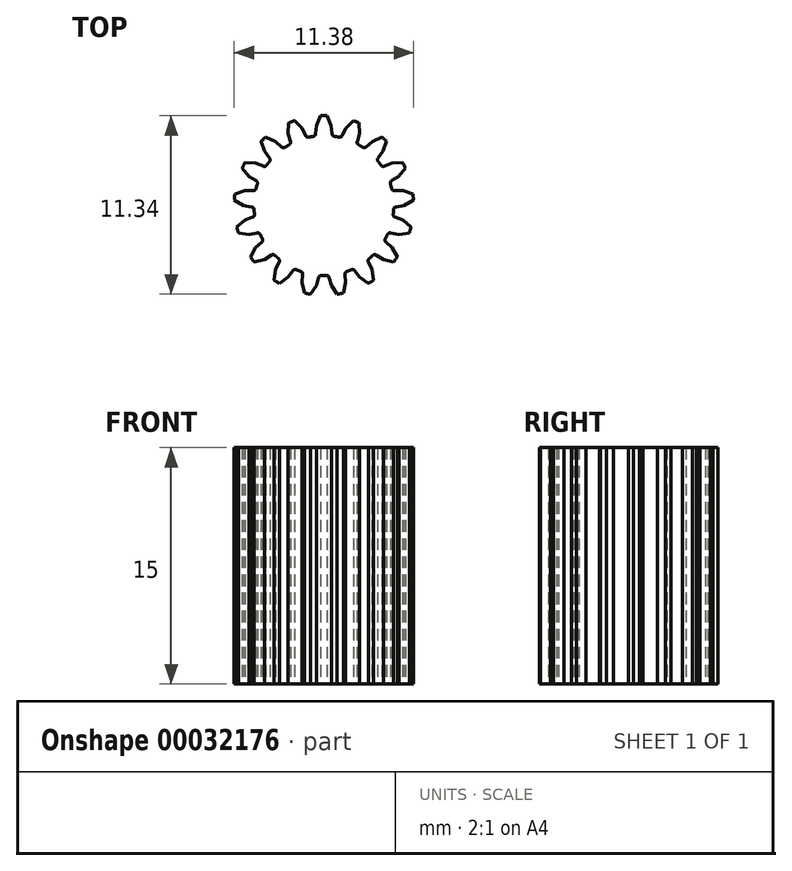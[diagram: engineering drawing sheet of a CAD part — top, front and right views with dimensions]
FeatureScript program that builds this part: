
annotation { "Feature Type Name" : "Feature", "Feature Type Description" : "" }
export const myFeature = defineFeature(function(context is Context, id is Id, definition is map)
    precondition{}
    {
        {
            var Q0;
            Q0=qCreatedBy(makeId("Top.planeOp"),FACE);
            var sketch = newSketch(context, id + "F0", { "sketchPlane" : qUnion([Q0])});
            skLineSegment(sketch, "E0", {"start": v(7.63, -0.2) * mm, "end": v(8.5, -0.04) * mm});
            skLineSegment(sketch, "E1", {"start": v(8.5, -0.04) * mm, "end": v(9.48, 0.5) * mm});
            skArc(sketch, "E2", {"start": v(9.48, 0.5) * mm, "mid": v(9.46, 0.82) * mm, "end": v(9.42, 1.15) * mm});
            skLineSegment(sketch, "E3", {"start": v(9.42, 1.15) * mm, "end": v(8.36, 1.5) * mm});
            skLineSegment(sketch, "E4", {"start": v(8.36, 1.5) * mm, "end": v(7.47, 1.5) * mm});
            skArc(sketch, "E5", {"start": v(7.18, 1.73) * mm, "mid": v(7.29, 1.56) * mm, "end": v(7.47, 1.5) * mm});
            skArc(sketch, "E6", {"start": v(7.18, 1.73) * mm, "mid": v(7.12, 1.97) * mm, "end": v(7.04, 2.21) * mm});
            skArc(sketch, "E7", {"start": v(7.17, 2.56) * mm, "mid": v(7.05, 2.4) * mm, "end": v(7.04, 2.21) * mm});
            skLineSegment(sketch, "E8", {"start": v(7.17, 2.56) * mm, "end": v(7.92, 3.03) * mm});
            skLineSegment(sketch, "E9", {"start": v(7.92, 3.03) * mm, "end": v(8.65, 3.88) * mm});
            skArc(sketch, "E10", {"start": v(8.65, 3.88) * mm, "mid": v(8.5, 4.18) * mm, "end": v(8.35, 4.48) * mm});
            skLineSegment(sketch, "E11", {"start": v(8.35, 4.48) * mm, "end": v(7.23, 4.41) * mm});
            skLineSegment(sketch, "E12", {"start": v(7.23, 4.41) * mm, "end": v(6.4, 4.1) * mm});
            skArc(sketch, "E13", {"start": v(6.05, 4.2) * mm, "mid": v(6.21, 4.09) * mm, "end": v(6.4, 4.1) * mm});
            skArc(sketch, "E14", {"start": v(6.05, 4.2) * mm, "mid": v(5.9, 4.4) * mm, "end": v(5.75, 4.6) * mm});
            skArc(sketch, "E15", {"start": v(5.74, 4.97) * mm, "mid": v(5.68, 4.79) * mm, "end": v(5.75, 4.6) * mm});
            skLineSegment(sketch, "E16", {"start": v(5.74, 4.97) * mm, "end": v(6.28, 5.68) * mm});
            skLineSegment(sketch, "E17", {"start": v(6.28, 5.68) * mm, "end": v(6.64, 6.74) * mm});
            skArc(sketch, "E18", {"start": v(6.64, 6.74) * mm, "mid": v(6.4, 6.97) * mm, "end": v(6.15, 7.19) * mm});
            skLineSegment(sketch, "E19", {"start": v(6.15, 7.19) * mm, "end": v(5.13, 6.72) * mm});
            skLineSegment(sketch, "E20", {"start": v(5.13, 6.72) * mm, "end": v(4.48, 6.13) * mm});
            skArc(sketch, "E21", {"start": v(4.1, 6.1) * mm, "mid": v(4.3, 6.05) * mm, "end": v(4.48, 6.13) * mm});
            skArc(sketch, "E22", {"start": v(4.1, 6.1) * mm, "mid": v(3.9, 6.24) * mm, "end": v(3.68, 6.37) * mm});
            skArc(sketch, "E23", {"start": v(3.54, 6.7) * mm, "mid": v(3.55, 6.51) * mm, "end": v(3.68, 6.37) * mm});
            skLineSegment(sketch, "E24", {"start": v(3.54, 6.7) * mm, "end": v(3.78, 7.56) * mm});
            skLineSegment(sketch, "E25", {"start": v(3.78, 7.56) * mm, "end": v(3.74, 8.68) * mm});
            skArc(sketch, "E26", {"start": v(3.74, 8.68) * mm, "mid": v(3.43, 8.8) * mm, "end": v(3.12, 8.92) * mm});
            skLineSegment(sketch, "E27", {"start": v(3.12, 8.92) * mm, "end": v(2.34, 8.12) * mm});
            skLineSegment(sketch, "E28", {"start": v(2.34, 8.12) * mm, "end": v(1.94, 7.33) * mm});
            skArc(sketch, "E29", {"start": v(1.6, 7.17) * mm, "mid": v(1.8, 7.2) * mm, "end": v(1.94, 7.33) * mm});
            skArc(sketch, "E30", {"start": v(1.6, 7.17) * mm, "mid": v(1.36, 7.22) * mm, "end": v(1.11, 7.26) * mm});
            skArc(sketch, "E31", {"start": v(0.86, 7.53) * mm, "mid": v(0.94, 7.35) * mm, "end": v(1.11, 7.26) * mm});
            skLineSegment(sketch, "E32", {"start": v(0.86, 7.53) * mm, "end": v(0.78, 8.41) * mm});
            skLineSegment(sketch, "E33", {"start": v(0.78, 8.41) * mm, "end": v(0.33, 9.44) * mm});
            skArc(sketch, "E34", {"start": v(0.33, 9.44) * mm, "mid": v(0, 9.45) * mm, "end": v(-0.33, 9.44) * mm});
            skLineSegment(sketch, "E35", {"start": v(-0.33, 9.44) * mm, "end": v(-0.78, 8.41) * mm});
            skLineSegment(sketch, "E36", {"start": v(-0.78, 8.41) * mm, "end": v(-0.86, 7.53) * mm});
            skArc(sketch, "E37", {"start": v(-1.11, 7.26) * mm, "mid": v(-0.94, 7.35) * mm, "end": v(-0.86, 7.53) * mm});
            skArc(sketch, "E38", {"start": v(-1.11, 7.26) * mm, "mid": v(-1.36, 7.22) * mm, "end": v(-1.6, 7.17) * mm});
            skArc(sketch, "E39", {"start": v(-1.94, 7.33) * mm, "mid": v(-1.8, 7.2) * mm, "end": v(-1.6, 7.17) * mm});
            skLineSegment(sketch, "E40", {"start": v(-1.94, 7.33) * mm, "end": v(-2.34, 8.12) * mm});
            skLineSegment(sketch, "E41", {"start": v(-2.34, 8.12) * mm, "end": v(-3.12, 8.92) * mm});
            skArc(sketch, "E42", {"start": v(-3.12, 8.92) * mm, "mid": v(-3.43, 8.8) * mm, "end": v(-3.74, 8.68) * mm});
            skLineSegment(sketch, "E43", {"start": v(-3.74, 8.68) * mm, "end": v(-3.78, 7.56) * mm});
            skLineSegment(sketch, "E44", {"start": v(-3.78, 7.56) * mm, "end": v(-3.54, 6.7) * mm});
            skArc(sketch, "E45", {"start": v(-3.68, 6.37) * mm, "mid": v(-3.55, 6.51) * mm, "end": v(-3.54, 6.7) * mm});
            skArc(sketch, "E46", {"start": v(-3.68, 6.37) * mm, "mid": v(-3.9, 6.24) * mm, "end": v(-4.1, 6.1) * mm});
            skArc(sketch, "E47", {"start": v(-4.48, 6.13) * mm, "mid": v(-4.3, 6.05) * mm, "end": v(-4.1, 6.1) * mm});
            skLineSegment(sketch, "E48", {"start": v(-4.48, 6.13) * mm, "end": v(-5.13, 6.72) * mm});
            skLineSegment(sketch, "E49", {"start": v(-5.13, 6.72) * mm, "end": v(-6.15, 7.19) * mm});
            skArc(sketch, "E50", {"start": v(-6.15, 7.19) * mm, "mid": v(-6.4, 6.97) * mm, "end": v(-6.64, 6.74) * mm});
            skLineSegment(sketch, "E51", {"start": v(-6.64, 6.74) * mm, "end": v(-6.28, 5.68) * mm});
            skLineSegment(sketch, "E52", {"start": v(-6.28, 5.68) * mm, "end": v(-5.74, 4.97) * mm});
            skArc(sketch, "E53", {"start": v(-5.75, 4.6) * mm, "mid": v(-5.68, 4.79) * mm, "end": v(-5.74, 4.97) * mm});
            skArc(sketch, "E54", {"start": v(-5.75, 4.6) * mm, "mid": v(-5.9, 4.4) * mm, "end": v(-6.05, 4.2) * mm});
            skArc(sketch, "E55", {"start": v(-6.4, 4.1) * mm, "mid": v(-6.21, 4.09) * mm, "end": v(-6.05, 4.2) * mm});
            skLineSegment(sketch, "E56", {"start": v(-6.4, 4.1) * mm, "end": v(-7.23, 4.41) * mm});
            skLineSegment(sketch, "E57", {"start": v(-7.23, 4.41) * mm, "end": v(-8.35, 4.48) * mm});
            skArc(sketch, "E58", {"start": v(-8.35, 4.48) * mm, "mid": v(-8.5, 4.18) * mm, "end": v(-8.65, 3.88) * mm});
            skLineSegment(sketch, "E59", {"start": v(-8.65, 3.88) * mm, "end": v(-7.92, 3.03) * mm});
            skLineSegment(sketch, "E60", {"start": v(-7.92, 3.03) * mm, "end": v(-7.17, 2.56) * mm});
            skArc(sketch, "E61", {"start": v(-7.04, 2.21) * mm, "mid": v(-7.05, 2.4) * mm, "end": v(-7.17, 2.56) * mm});
            skArc(sketch, "E62", {"start": v(-7.04, 2.21) * mm, "mid": v(-7.12, 1.97) * mm, "end": v(-7.18, 1.73) * mm});
            skArc(sketch, "E63", {"start": v(-7.47, 1.5) * mm, "mid": v(-7.29, 1.56) * mm, "end": v(-7.18, 1.73) * mm});
            skLineSegment(sketch, "E64", {"start": v(-7.47, 1.5) * mm, "end": v(-8.36, 1.5) * mm});
            skLineSegment(sketch, "E65", {"start": v(-8.36, 1.5) * mm, "end": v(-9.42, 1.15) * mm});
            skArc(sketch, "E66", {"start": v(-9.42, 1.15) * mm, "mid": v(-9.46, 0.82) * mm, "end": v(-9.48, 0.5) * mm});
            skLineSegment(sketch, "E67", {"start": v(-9.48, 0.5) * mm, "end": v(-8.5, -0.04) * mm});
            skLineSegment(sketch, "E68", {"start": v(-8.5, -0.04) * mm, "end": v(-7.63, -0.2) * mm});
            skArc(sketch, "E69", {"start": v(-7.39, -0.48) * mm, "mid": v(-7.46, -0.3) * mm, "end": v(-7.63, -0.2) * mm});
            skArc(sketch, "E70", {"start": v(-7.39, -0.48) * mm, "mid": v(-7.37, -0.74) * mm, "end": v(-7.34, -0.99) * mm});
            skArc(sketch, "E71", {"start": v(-7.53, -1.3) * mm, "mid": v(-7.38, -1.18) * mm, "end": v(-7.34, -0.99) * mm});
            skLineSegment(sketch, "E72", {"start": v(-7.53, -1.3) * mm, "end": v(-8.35, -1.62) * mm});
            skLineSegment(sketch, "E73", {"start": v(-8.35, -1.62) * mm, "end": v(-9.22, -2.33) * mm});
            skArc(sketch, "E74", {"start": v(-9.22, -2.33) * mm, "mid": v(-9.14, -2.65) * mm, "end": v(-9.04, -2.97) * mm});
            skLineSegment(sketch, "E75", {"start": v(-9.04, -2.97) * mm, "end": v(-7.93, -3.11) * mm});
            skLineSegment(sketch, "E76", {"start": v(-7.93, -3.11) * mm, "end": v(-7.06, -2.95) * mm});
            skArc(sketch, "E77", {"start": v(-6.73, -3.12) * mm, "mid": v(-6.87, -2.98) * mm, "end": v(-7.06, -2.95) * mm});
            skArc(sketch, "E78", {"start": v(-6.73, -3.12) * mm, "mid": v(-6.62, -3.35) * mm, "end": v(-6.5, -3.58) * mm});
            skArc(sketch, "E79", {"start": v(-6.57, -3.94) * mm, "mid": v(-6.48, -3.77) * mm, "end": v(-6.5, -3.58) * mm});
            skLineSegment(sketch, "E80", {"start": v(-6.57, -3.94) * mm, "end": v(-7.22, -4.54) * mm});
            skLineSegment(sketch, "E81", {"start": v(-7.22, -4.54) * mm, "end": v(-7.78, -5.5) * mm});
            skArc(sketch, "E82", {"start": v(-7.78, -5.5) * mm, "mid": v(-7.58, -5.78) * mm, "end": v(-7.38, -6.04) * mm});
            skLineSegment(sketch, "E83", {"start": v(-7.38, -6.04) * mm, "end": v(-6.29, -5.77) * mm});
            skLineSegment(sketch, "E84", {"start": v(-6.29, -5.77) * mm, "end": v(-5.54, -5.3) * mm});
            skArc(sketch, "E85", {"start": v(-5.17, -5.35) * mm, "mid": v(-5.35, -5.27) * mm, "end": v(-5.54, -5.3) * mm});
            skArc(sketch, "E86", {"start": v(-5.17, -5.35) * mm, "mid": v(-4.99, -5.52) * mm, "end": v(-4.8, -5.69) * mm});
            skArc(sketch, "E87", {"start": v(-4.72, -6.05) * mm, "mid": v(-4.7, -5.86) * mm, "end": v(-4.8, -5.69) * mm});
            skLineSegment(sketch, "E88", {"start": v(-4.72, -6.05) * mm, "end": v(-5.11, -6.84) * mm});
            skLineSegment(sketch, "E89", {"start": v(-5.11, -6.84) * mm, "end": v(-5.28, -7.95) * mm});
            skArc(sketch, "E90", {"start": v(-5.28, -7.95) * mm, "mid": v(-5, -8.13) * mm, "end": v(-4.71, -8.3) * mm});
            skLineSegment(sketch, "E91", {"start": v(-4.71, -8.3) * mm, "end": v(-3.8, -7.66) * mm});
            skLineSegment(sketch, "E92", {"start": v(-3.8, -7.66) * mm, "end": v(-3.26, -6.95) * mm});
            skArc(sketch, "E93", {"start": v(-2.9, -6.86) * mm, "mid": v(-3.1, -6.84) * mm, "end": v(-3.26, -6.95) * mm});
            skArc(sketch, "E94", {"start": v(-2.9, -6.86) * mm, "mid": v(-2.67, -6.95) * mm, "end": v(-2.44, -7.04) * mm});
            skArc(sketch, "E95", {"start": v(-2.24, -7.35) * mm, "mid": v(-2.28, -7.16) * mm, "end": v(-2.44, -7.04) * mm});
            skLineSegment(sketch, "E96", {"start": v(-2.24, -7.35) * mm, "end": v(-2.32, -8.23) * mm});
            skLineSegment(sketch, "E97", {"start": v(-2.32, -8.23) * mm, "end": v(-2.07, -9.32) * mm});
            skArc(sketch, "E98", {"start": v(-2.07, -9.32) * mm, "mid": v(-1.75, -9.4) * mm, "end": v(-1.42, -9.45) * mm});
            skLineSegment(sketch, "E99", {"start": v(-1.42, -9.45) * mm, "end": v(-0.8, -8.52) * mm});
            skLineSegment(sketch, "E100", {"start": v(-0.8, -8.52) * mm, "end": v(-0.55, -7.67) * mm});
            skArc(sketch, "E101", {"start": v(-0.25, -7.45) * mm, "mid": v(-0.44, -7.5) * mm, "end": v(-0.55, -7.67) * mm});
            skArc(sketch, "E102", {"start": v(-0.25, -7.45) * mm, "mid": v(0, -7.45) * mm, "end": v(0.25, -7.45) * mm});
            skArc(sketch, "E103", {"start": v(0.55, -7.67) * mm, "mid": v(0.44, -7.5) * mm, "end": v(0.25, -7.45) * mm});
            skLineSegment(sketch, "E104", {"start": v(0.55, -7.67) * mm, "end": v(0.8, -8.52) * mm});
            skLineSegment(sketch, "E105", {"start": v(0.8, -8.52) * mm, "end": v(1.42, -9.45) * mm});
            skArc(sketch, "E106", {"start": v(1.42, -9.45) * mm, "mid": v(1.75, -9.4) * mm, "end": v(2.07, -9.32) * mm});
            skLineSegment(sketch, "E107", {"start": v(2.07, -9.32) * mm, "end": v(2.32, -8.23) * mm});
            skLineSegment(sketch, "E108", {"start": v(2.32, -8.23) * mm, "end": v(2.24, -7.35) * mm});
            skArc(sketch, "E109", {"start": v(2.44, -7.04) * mm, "mid": v(2.28, -7.16) * mm, "end": v(2.24, -7.35) * mm});
            skArc(sketch, "E110", {"start": v(2.44, -7.04) * mm, "mid": v(2.67, -6.95) * mm, "end": v(2.9, -6.86) * mm});
            skArc(sketch, "E111", {"start": v(3.26, -6.95) * mm, "mid": v(3.1, -6.84) * mm, "end": v(2.9, -6.86) * mm});
            skLineSegment(sketch, "E112", {"start": v(3.26, -6.95) * mm, "end": v(3.8, -7.66) * mm});
            skLineSegment(sketch, "E113", {"start": v(3.8, -7.66) * mm, "end": v(4.71, -8.3) * mm});
            skArc(sketch, "E114", {"start": v(4.71, -8.3) * mm, "mid": v(5, -8.13) * mm, "end": v(5.28, -7.95) * mm});
            skLineSegment(sketch, "E115", {"start": v(5.28, -7.95) * mm, "end": v(5.11, -6.84) * mm});
            skLineSegment(sketch, "E116", {"start": v(5.11, -6.84) * mm, "end": v(4.72, -6.05) * mm});
            skArc(sketch, "E117", {"start": v(4.8, -5.69) * mm, "mid": v(4.7, -5.86) * mm, "end": v(4.72, -6.05) * mm});
            skArc(sketch, "E118", {"start": v(4.8, -5.69) * mm, "mid": v(4.99, -5.52) * mm, "end": v(5.17, -5.35) * mm});
            skArc(sketch, "E119", {"start": v(5.54, -5.3) * mm, "mid": v(5.35, -5.27) * mm, "end": v(5.17, -5.35) * mm});
            skLineSegment(sketch, "E120", {"start": v(5.54, -5.3) * mm, "end": v(6.29, -5.77) * mm});
            skLineSegment(sketch, "E121", {"start": v(6.29, -5.77) * mm, "end": v(7.38, -6.04) * mm});
            skArc(sketch, "E122", {"start": v(7.38, -6.04) * mm, "mid": v(7.58, -5.78) * mm, "end": v(7.78, -5.5) * mm});
            skLineSegment(sketch, "E123", {"start": v(7.78, -5.5) * mm, "end": v(7.22, -4.54) * mm});
            skLineSegment(sketch, "E124", {"start": v(7.22, -4.54) * mm, "end": v(6.57, -3.94) * mm});
            skArc(sketch, "E125", {"start": v(6.5, -3.58) * mm, "mid": v(6.48, -3.77) * mm, "end": v(6.57, -3.94) * mm});
            skArc(sketch, "E126", {"start": v(6.5, -3.58) * mm, "mid": v(6.62, -3.35) * mm, "end": v(6.73, -3.12) * mm});
            skArc(sketch, "E127", {"start": v(7.06, -2.95) * mm, "mid": v(6.87, -2.98) * mm, "end": v(6.73, -3.12) * mm});
            skLineSegment(sketch, "E128", {"start": v(7.06, -2.95) * mm, "end": v(7.93, -3.11) * mm});
            skLineSegment(sketch, "E129", {"start": v(7.93, -3.11) * mm, "end": v(9.04, -2.97) * mm});
            skArc(sketch, "E130", {"start": v(9.04, -2.97) * mm, "mid": v(9.14, -2.65) * mm, "end": v(9.22, -2.33) * mm});
            skLineSegment(sketch, "E131", {"start": v(9.22, -2.33) * mm, "end": v(8.35, -1.62) * mm});
            skLineSegment(sketch, "E132", {"start": v(8.35, -1.62) * mm, "end": v(7.53, -1.3) * mm});
            skArc(sketch, "E133", {"start": v(7.34, -0.99) * mm, "mid": v(7.38, -1.18) * mm, "end": v(7.53, -1.3) * mm});
            skArc(sketch, "E134", {"start": v(7.34, -0.99) * mm, "mid": v(7.37, -0.74) * mm, "end": v(7.39, -0.48) * mm});
            skArc(sketch, "E135", {"start": v(7.63, -0.2) * mm, "mid": v(7.46, -0.3) * mm, "end": v(7.39, -0.48) * mm});
            skSolve(sketch);
        }
        {
            var Q0;
            Q0=makeQuery(id+"F0.imprint","IMPRINT",FACE,{"disambiguationData":[TD([[makeQuery(id+"F0.imprint","IMPRINT",EDGE,{"derivedFrom":sQuery(id+"F0.wireOp",EDGE,"E0")}),1.0]])]});
            extrude(context, id + "F1", {"entities" : qUnion([Q0]), "depth" : 25 * mm});
        }
        {
            var Q0;
            Q0=makeQuery(id+"F1.opExtrude","SWEPT_BODY",BODY,{"disambiguationData":[OSD([sQuery(id+"F0.wireOp",EDGE,"E0"),sQuery(id+"F0.wireOp",EDGE,"E1"),sQuery(id+"F0.wireOp",EDGE,"E2"),sQuery(id+"F0.wireOp",EDGE,"E3"),sQuery(id+"F0.wireOp",EDGE,"E4"),sQuery(id+"F0.wireOp",EDGE,"E5"),sQuery(id+"F0.wireOp",EDGE,"E6"),sQuery(id+"F0.wireOp",EDGE,"E7"),sQuery(id+"F0.wireOp",EDGE,"E8"),sQuery(id+"F0.wireOp",EDGE,"E9"),sQuery(id+"F0.wireOp",EDGE,"E10"),sQuery(id+"F0.wireOp",EDGE,"E11"),sQuery(id+"F0.wireOp",EDGE,"E12"),sQuery(id+"F0.wireOp",EDGE,"E13"),sQuery(id+"F0.wireOp",EDGE,"E14"),sQuery(id+"F0.wireOp",EDGE,"E15"),sQuery(id+"F0.wireOp",EDGE,"E16"),sQuery(id+"F0.wireOp",EDGE,"E17"),sQuery(id+"F0.wireOp",EDGE,"E18"),sQuery(id+"F0.wireOp",EDGE,"E19"),sQuery(id+"F0.wireOp",EDGE,"E20"),sQuery(id+"F0.wireOp",EDGE,"E21"),sQuery(id+"F0.wireOp",EDGE,"E22"),sQuery(id+"F0.wireOp",EDGE,"E23"),sQuery(id+"F0.wireOp",EDGE,"E24"),sQuery(id+"F0.wireOp",EDGE,"E25"),sQuery(id+"F0.wireOp",EDGE,"E26"),sQuery(id+"F0.wireOp",EDGE,"E27"),sQuery(id+"F0.wireOp",EDGE,"E28"),sQuery(id+"F0.wireOp",EDGE,"E29"),sQuery(id+"F0.wireOp",EDGE,"E30"),sQuery(id+"F0.wireOp",EDGE,"E31"),sQuery(id+"F0.wireOp",EDGE,"E32"),sQuery(id+"F0.wireOp",EDGE,"E33"),sQuery(id+"F0.wireOp",EDGE,"E34"),sQuery(id+"F0.wireOp",EDGE,"E35"),sQuery(id+"F0.wireOp",EDGE,"E36"),sQuery(id+"F0.wireOp",EDGE,"E37"),sQuery(id+"F0.wireOp",EDGE,"E38"),sQuery(id+"F0.wireOp",EDGE,"E39"),sQuery(id+"F0.wireOp",EDGE,"E40"),sQuery(id+"F0.wireOp",EDGE,"E41"),sQuery(id+"F0.wireOp",EDGE,"E42"),sQuery(id+"F0.wireOp",EDGE,"E43"),sQuery(id+"F0.wireOp",EDGE,"E44"),sQuery(id+"F0.wireOp",EDGE,"E45"),sQuery(id+"F0.wireOp",EDGE,"E46"),sQuery(id+"F0.wireOp",EDGE,"E47"),sQuery(id+"F0.wireOp",EDGE,"E48"),sQuery(id+"F0.wireOp",EDGE,"E49"),sQuery(id+"F0.wireOp",EDGE,"E50"),sQuery(id+"F0.wireOp",EDGE,"E51"),sQuery(id+"F0.wireOp",EDGE,"E52"),sQuery(id+"F0.wireOp",EDGE,"E53"),sQuery(id+"F0.wireOp",EDGE,"E54"),sQuery(id+"F0.wireOp",EDGE,"E55"),sQuery(id+"F0.wireOp",EDGE,"E56"),sQuery(id+"F0.wireOp",EDGE,"E57"),sQuery(id+"F0.wireOp",EDGE,"E58"),sQuery(id+"F0.wireOp",EDGE,"E59"),sQuery(id+"F0.wireOp",EDGE,"E60"),sQuery(id+"F0.wireOp",EDGE,"E61"),sQuery(id+"F0.wireOp",EDGE,"E62"),sQuery(id+"F0.wireOp",EDGE,"E63"),sQuery(id+"F0.wireOp",EDGE,"E64"),sQuery(id+"F0.wireOp",EDGE,"E65"),sQuery(id+"F0.wireOp",EDGE,"E66"),sQuery(id+"F0.wireOp",EDGE,"E67"),sQuery(id+"F0.wireOp",EDGE,"E68"),sQuery(id+"F0.wireOp",EDGE,"E69"),sQuery(id+"F0.wireOp",EDGE,"E70"),sQuery(id+"F0.wireOp",EDGE,"E71"),sQuery(id+"F0.wireOp",EDGE,"E72"),sQuery(id+"F0.wireOp",EDGE,"E73"),sQuery(id+"F0.wireOp",EDGE,"E74"),sQuery(id+"F0.wireOp",EDGE,"E75"),sQuery(id+"F0.wireOp",EDGE,"E76"),sQuery(id+"F0.wireOp",EDGE,"E77"),sQuery(id+"F0.wireOp",EDGE,"E78"),sQuery(id+"F0.wireOp",EDGE,"E79"),sQuery(id+"F0.wireOp",EDGE,"E80"),sQuery(id+"F0.wireOp",EDGE,"E81"),sQuery(id+"F0.wireOp",EDGE,"E82"),sQuery(id+"F0.wireOp",EDGE,"E83"),sQuery(id+"F0.wireOp",EDGE,"E84"),sQuery(id+"F0.wireOp",EDGE,"E85"),sQuery(id+"F0.wireOp",EDGE,"E86"),sQuery(id+"F0.wireOp",EDGE,"E87"),sQuery(id+"F0.wireOp",EDGE,"E88"),sQuery(id+"F0.wireOp",EDGE,"E89"),sQuery(id+"F0.wireOp",EDGE,"E90"),sQuery(id+"F0.wireOp",EDGE,"E91"),sQuery(id+"F0.wireOp",EDGE,"E92"),sQuery(id+"F0.wireOp",EDGE,"E93"),sQuery(id+"F0.wireOp",EDGE,"E94"),sQuery(id+"F0.wireOp",EDGE,"E95"),sQuery(id+"F0.wireOp",EDGE,"E96"),sQuery(id+"F0.wireOp",EDGE,"E97"),sQuery(id+"F0.wireOp",EDGE,"E98"),sQuery(id+"F0.wireOp",EDGE,"E99"),sQuery(id+"F0.wireOp",EDGE,"E100"),sQuery(id+"F0.wireOp",EDGE,"E101"),sQuery(id+"F0.wireOp",EDGE,"E102"),sQuery(id+"F0.wireOp",EDGE,"E103"),sQuery(id+"F0.wireOp",EDGE,"E104"),sQuery(id+"F0.wireOp",EDGE,"E105"),sQuery(id+"F0.wireOp",EDGE,"E106"),sQuery(id+"F0.wireOp",EDGE,"E107"),sQuery(id+"F0.wireOp",EDGE,"E108"),sQuery(id+"F0.wireOp",EDGE,"E109"),sQuery(id+"F0.wireOp",EDGE,"E110"),sQuery(id+"F0.wireOp",EDGE,"E111"),sQuery(id+"F0.wireOp",EDGE,"E112"),sQuery(id+"F0.wireOp",EDGE,"E113"),sQuery(id+"F0.wireOp",EDGE,"E114"),sQuery(id+"F0.wireOp",EDGE,"E115"),sQuery(id+"F0.wireOp",EDGE,"E116"),sQuery(id+"F0.wireOp",EDGE,"E117"),sQuery(id+"F0.wireOp",EDGE,"E118"),sQuery(id+"F0.wireOp",EDGE,"E119"),sQuery(id+"F0.wireOp",EDGE,"E120"),sQuery(id+"F0.wireOp",EDGE,"E121"),sQuery(id+"F0.wireOp",EDGE,"E122"),sQuery(id+"F0.wireOp",EDGE,"E123"),sQuery(id+"F0.wireOp",EDGE,"E124"),sQuery(id+"F0.wireOp",EDGE,"E125"),sQuery(id+"F0.wireOp",EDGE,"E126"),sQuery(id+"F0.wireOp",EDGE,"E127"),sQuery(id+"F0.wireOp",EDGE,"E128"),sQuery(id+"F0.wireOp",EDGE,"E129"),sQuery(id+"F0.wireOp",EDGE,"E130"),sQuery(id+"F0.wireOp",EDGE,"E131"),sQuery(id+"F0.wireOp",EDGE,"E132"),sQuery(id+"F0.wireOp",EDGE,"E133"),sQuery(id+"F0.wireOp",EDGE,"E134"),sQuery(id+"F0.wireOp",EDGE,"E135")])]});
            var Q1;
            Q1=qCreatedBy(makeId("Origin.pointOp"),VERTEX);
            transform(context, id + "F2", {"entities" : qUnion([Q0]), "transformType" : TransformType.SCALE_UNIFORMLY, "scale" : .6, "makeCopy" : false, "scalePoint" : qUnion([Q1])});
        }
    });
